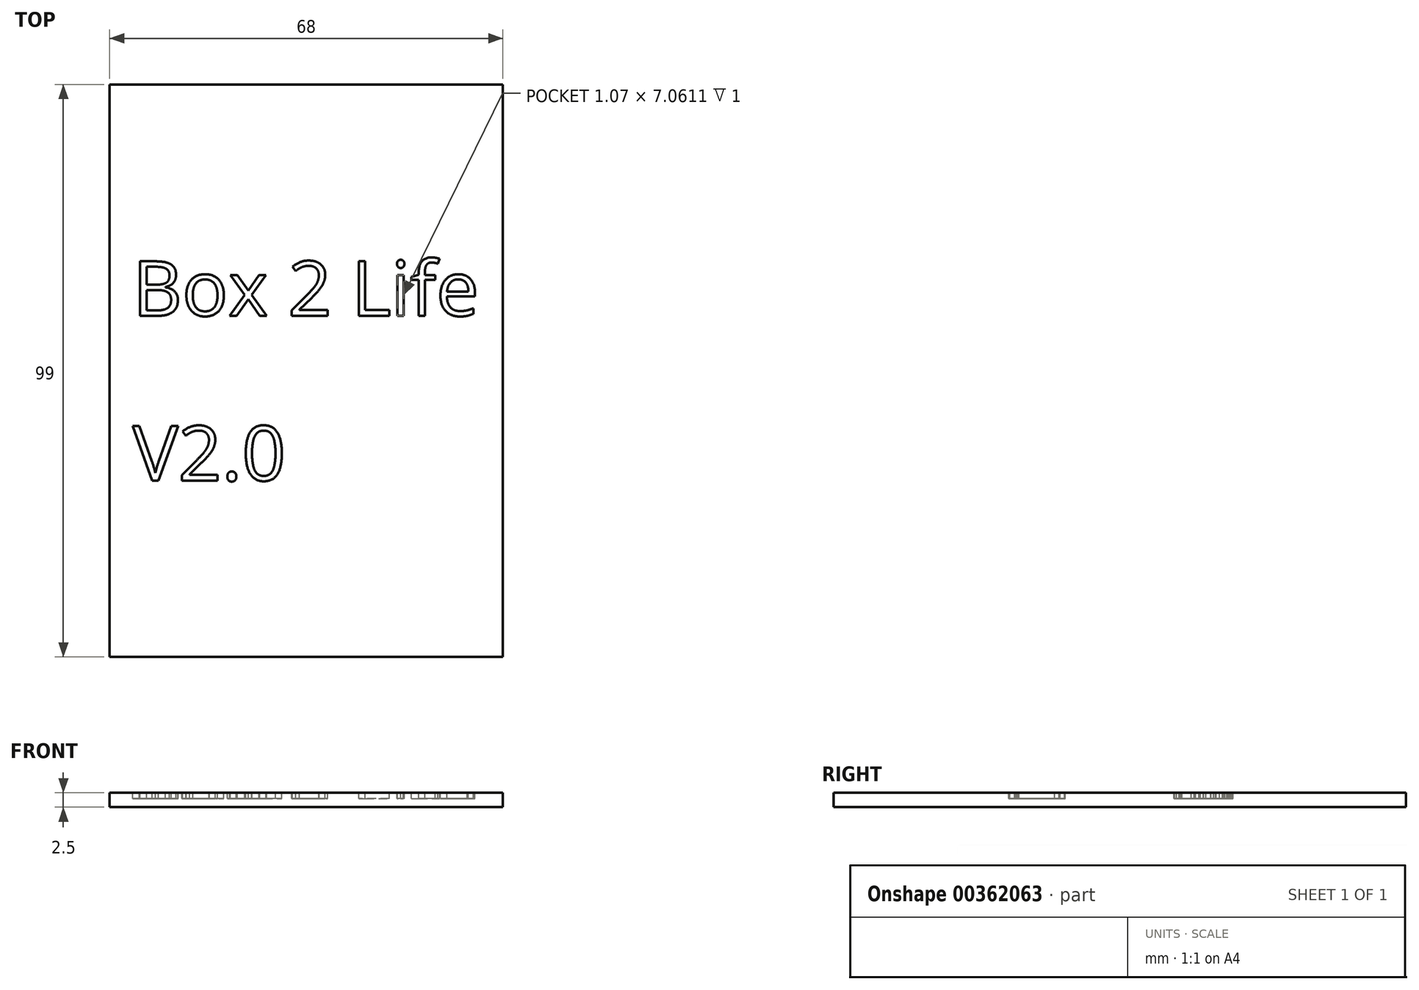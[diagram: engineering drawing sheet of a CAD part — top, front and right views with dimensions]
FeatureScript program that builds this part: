
annotation { "Feature Type Name" : "Feature", "Feature Type Description" : "" }
export const myFeature = defineFeature(function(context is Context, id is Id, definition is map)
    precondition{}
    {
        {
            var Q0;
            Q0=qCreatedBy(makeId("Top.planeOp"),FACE);
            var sketch = newSketch(context, id + "F0", { "sketchPlane" : qUnion([Q0])});
            skLineSegment(sketch, "E0.bottom", {"start": v(0, 0) * mm, "end": v(68, 0) * mm});
            skLineSegment(sketch, "E0.top", {"start": v(0, 99) * mm, "end": v(68, 99) * mm});
            skLineSegment(sketch, "E0.left", {"start": v(0, 0) * mm, "end": v(0, 99) * mm});
            skLineSegment(sketch, "E0.right", {"start": v(68, 0) * mm, "end": v(68, 99) * mm});
            skSolve(sketch);
        }
        {
            var Q0;
            Q0 = qSketchRegion(id + "F0", true);
            extrude(context, id + "F1", {"entities" : qUnion([Q0]), "depth" : 2.5 * mm});
        }
        {
            var Q0;
            Q0=makeQuery(id+"F1.opExtrude","CAP_FACE",FACE,{"disambiguationData":[OSD([sQuery(id+"F0.wireOp",EDGE,"E0.bottom"),sQuery(id+"F0.wireOp",EDGE,"E0.top"),sQuery(id+"F0.wireOp",EDGE,"E0.left"),sQuery(id+"F0.wireOp",EDGE,"E0.right")])],"isStart":false});
            var sketch = newSketch(context, id + "F2", { "sketchPlane" : qUnion([Q0])});
            skText(sketch, "E1", { "text": "Box 2 Life", "fontName": "OpenSans-Regular.ttf"});
            skText(sketch, "E2", { "text": "V2.0", "fontName": "OpenSans-Regular.ttf"});
            skLineSegment(sketch, "E3", {"start": v(3.97, 40) * mm, "end": v(3.97, 59) * mm, "construction": true});
            skLineSegment(sketch, "E4", {"start": v(34, 68.5) * mm, "end": v(34, 99) * mm, "construction": true});
            skPoint(sketch, "E5", {"position": v(3.97, 49.5) * mm});
            const initialGuessF2  = {"E1": [0.00397, 0.059, 1, 0, 0.0095], "E2": [0.00397, 0.0305, 1, 0, 0.0095]};
            skSetInitialGuess(sketch, initialGuessF2);
            skSolve(sketch);
        }
        {
            var Q0;
            Q0 = qSketchRegion(id + "F2", true);
            extrude(context, id + "F3", {"entities" : qUnion([Q0]), "operationType" : NewBodyOperationType.REMOVE, "oppositeDirection" : true, "depth" : 1 * mm});
        }
    });
